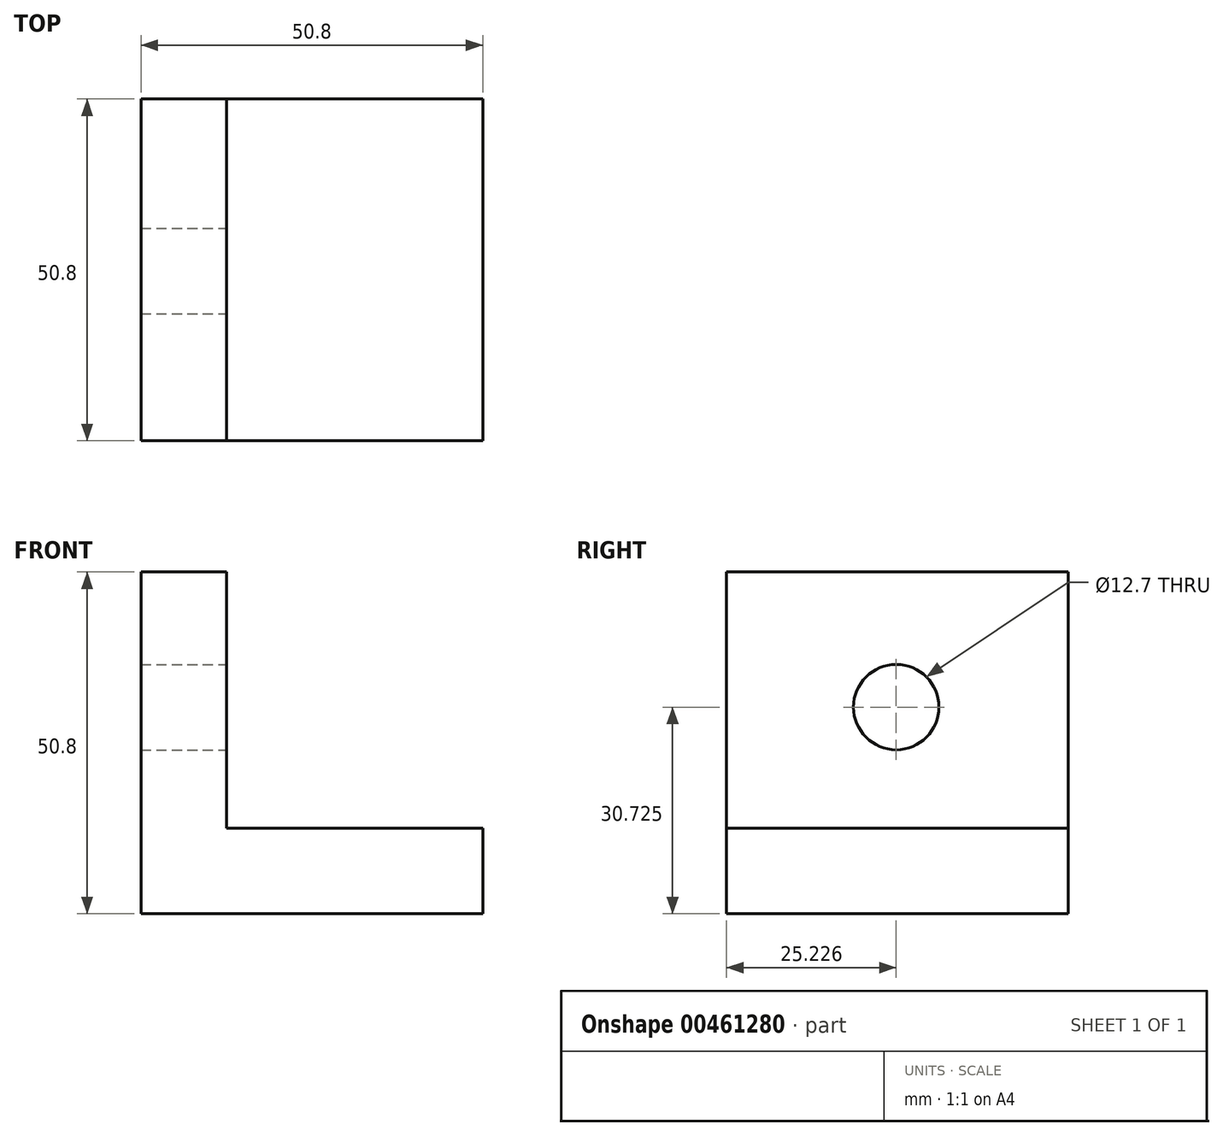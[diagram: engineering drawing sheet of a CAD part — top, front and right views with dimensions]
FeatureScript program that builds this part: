
annotation { "Feature Type Name" : "Feature", "Feature Type Description" : "" }
export const myFeature = defineFeature(function(context is Context, id is Id, definition is map)
    precondition{}
    {
        {
            var Q0;
            Q0=qCreatedBy(makeId("Top.planeOp"),FACE);
            var sketch = newSketch(context, id + "F0", { "sketchPlane" : qUnion([Q0])});
            skLineSegment(sketch, "E0.bottom", {"start": v(-25.07, 34.37) * mm, "end": v(25.73, 34.37) * mm});
            skLineSegment(sketch, "E0.top", {"start": v(-25.07, -16.43) * mm, "end": v(25.73, -16.43) * mm});
            skLineSegment(sketch, "E0.left", {"start": v(-25.07, 34.37) * mm, "end": v(-25.07, -16.43) * mm});
            skLineSegment(sketch, "E0.right", {"start": v(25.73, 34.37) * mm, "end": v(25.73, -16.43) * mm});
            skSolve(sketch);
        }
        {
            var Q0;
            Q0 = qSketchRegion(id + "F0", true);
            extrude(context, id + "F1", {"entities" : qUnion([Q0]), "depth" : 12.7 * mm});
        }
        {
            var Q0;
            Q0=makeQuery(id+"F1.opExtrude","CAP_FACE",FACE,{"disambiguationData":[OSD([sQuery(id+"F0.wireOp",EDGE,"E0.bottom"),sQuery(id+"F0.wireOp",EDGE,"E0.top"),sQuery(id+"F0.wireOp",EDGE,"E0.left"),sQuery(id+"F0.wireOp",EDGE,"E0.right")])],"isStart":false});
            var sketch = newSketch(context, id + "F2", { "sketchPlane" : qUnion([Q0])});
            skLineSegment(sketch, "E1.bottom", {"start": v(-25.07, 34.37) * mm, "end": v(-12.37, 34.37) * mm});
            skLineSegment(sketch, "E1.top", {"start": v(-25.07, -16.43) * mm, "end": v(-12.37, -16.43) * mm});
            skLineSegment(sketch, "E1.left", {"start": v(-25.07, 34.37) * mm, "end": v(-25.07, -16.43) * mm});
            skLineSegment(sketch, "E1.right", {"start": v(-12.37, 34.37) * mm, "end": v(-12.37, -16.43) * mm});
            skSolve(sketch);
        }
        {
            var Q0;
            Q0 = qSketchRegion(id + "F2", true);
            extrude(context, id + "F3", {"entities" : qUnion([Q0]), "operationType" : NewBodyOperationType.ADD, "depth" : 38.1 * mm});
        }
        {
            var Q0;
            Q0=makeQuery(id+"F3.opExtrude","SWEPT_FACE",FACE,{"disambiguationData":[OSD([sQuery(id+"F2.wireOp",EDGE,"E1.right")])]});
            var sketch = newSketch(context, id + "F4", { "sketchPlane" : qUnion([Q0])});
            skCircle(sketch, "E2", {"center": v(8.8, 30.73) * mm, "radius": 6.35 * mm});
            skSolve(sketch);
        }
        {
            var Q0;
            Q0=makeQuery(id+"F4.imprint","IMPRINT",FACE,{"disambiguationData":[TD([[makeQuery(id+"F4.imprint","IMPRINT",EDGE,{"derivedFrom":sQuery(id+"F4.wireOp",EDGE,"E2")}),1.0]])]});
            extrude(context, id + "F5", {"entities" : qUnion([Q0]), "operationType" : NewBodyOperationType.REMOVE, "oppositeDirection" : true, "depth" : 25.4 * mm});
        }
    });
